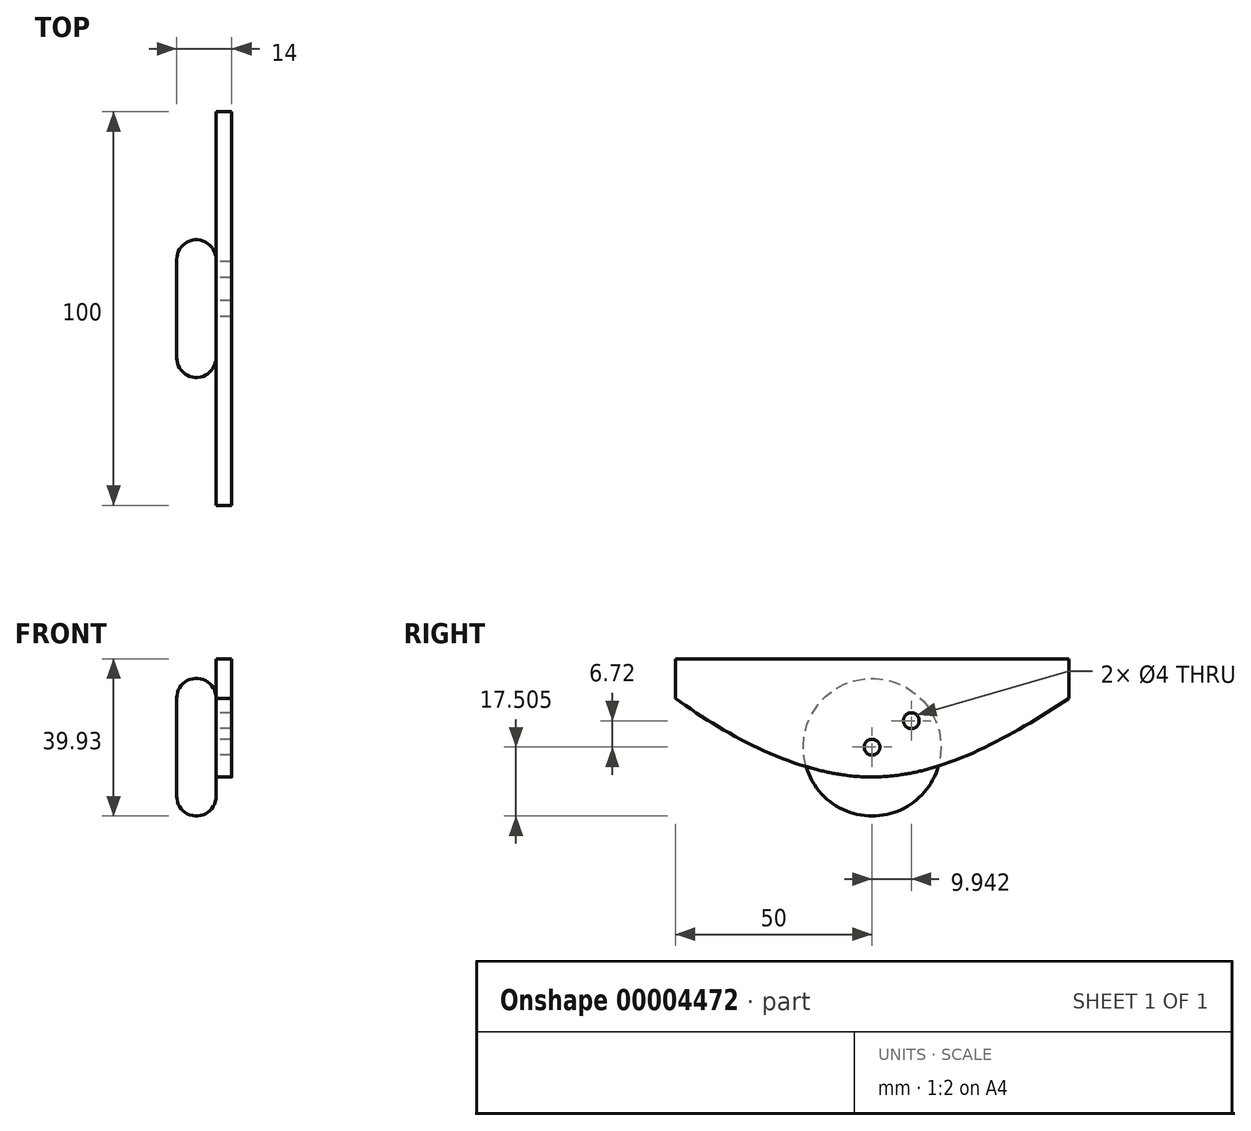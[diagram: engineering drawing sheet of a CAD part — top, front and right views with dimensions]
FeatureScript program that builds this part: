
annotation { "Feature Type Name" : "Feature", "Feature Type Description" : "" }
export const myFeature = defineFeature(function(context is Context, id is Id, definition is map)
    precondition{}
    {
        {
            var Q0;
            Q0=qCreatedBy(makeId("Right.planeOp"),FACE);
            var sketch = newSketch(context, id + "F0", { "sketchPlane" : qUnion([Q0])});
            skFitSpline(sketch, "E0", {"points": [v(-50, 0) * mm, v(0, -20) * mm, v(50, 0) * mm], "startDerivative": vector(87.23, -63) * mm, "endDerivative": vector(94.66, 62.2) * mm});
            skLineSegment(sketch, "E1", {"start": v(-50, 0) * mm, "end": v(-50, 10) * mm});
            skLineSegment(sketch, "E2", {"start": v(-50, 10) * mm, "end": v(50, 10) * mm});
            skLineSegment(sketch, "E3", {"start": v(50, 10) * mm, "end": v(50, 0) * mm});
            skCircle(sketch, "E4", {"center": v(0, -12.43) * mm, "radius": 17.5 * mm});
            skCircle(sketch, "E5", {"center": v(0, -12.43) * mm, "radius": 2 * mm});
            skCircle(sketch, "E6", {"center": v(0, -12.43) * mm, "radius": 10 * mm});
            skCircle(sketch, "E7", {"center": v(9.94, -5.7) * mm, "radius": 2 * mm});
            skCircle(sketch, "E8", {"center": v(9.94, -5.7) * mm, "radius": 1.25 * mm});
            skPoint(sketch, "E9", {"position": v(0, 10) * mm});
            skSolve(sketch);
        }
        {
            var Q0;
            {var subQ4=sQuery(id+"F0.wireOp",EDGE,"E1");Q0=makeQuery(id+"F0.imprint","IMPRINT",FACE,{"disambiguationData":[TD([[makeQuery(id+"F0.imprint","IMPRINT",EDGE,{"derivedFrom":subQ4}),-1.0]])]});}
            var Q1;
            {var subQ0=sQuery(id+"F0.wireOp",EDGE,"E7");Q1=makeQuery(id+"F0.imprint","IMPRINT",FACE,{"disambiguationData":[TD([[makeQuery(id+"F0.imprint","IMPRINT",EDGE,{"derivedFrom":subQ0}),-1.0]])]});}
            var Q2;
            Q2=makeQuery(id+"F0.imprint","IMPRINT",FACE,{"disambiguationData":[TD([[makeQuery(id+"F0.imprint","IMPRINT",EDGE,{"derivedFrom":sQuery(id+"F0.wireOp",EDGE,"E5")}),-1.0]])]});
            extrude(context, id + "F1", {"entities" : qUnion([Q0, Q1, Q2]), "depth" : 4 * mm});
        }
        {
            var Q0;
            Q0=makeQuery(id+"F0.imprint","IMPRINT",FACE,{"disambiguationData":[TD([[makeQuery(id+"F0.imprint","IMPRINT",EDGE,{"derivedFrom":sQuery(id+"F0.wireOp",EDGE,"E5")}),1.0]])]});
            var Q1;
            {var subQ0=sQuery(id+"F0.wireOp",EDGE,"E6");var subQ1=sQuery(id+"F0.wireOp",EDGE,"E0");var subQ3=makeQuery(id+"F0.imprint","INTERSECT",VERTEX,{"disambiguationData":[OD(0.0)],"derivedFrom":[subQ1,subQ0]});Q1=makeQuery(id+"F0.imprint","IMPRINT",FACE,{"disambiguationData":[TD([[makeQuery(id+"F0.imprint","IMPRINT",EDGE,{"disambiguationData":[TD([[subQ3,-1.0]])],"derivedFrom":subQ1}),-1.0]])]});}
            var Q2;
            {var subQ0=sQuery(id+"F0.wireOp",EDGE,"E7");Q2=makeQuery(id+"F0.imprint","IMPRINT",FACE,{"disambiguationData":[TD([[makeQuery(id+"F0.imprint","IMPRINT",EDGE,{"derivedFrom":subQ0}),-1.0]])]});}
            var Q3;
            {var subQ0=sQuery(id+"F0.wireOp",EDGE,"E4");var subQ1=sQuery(id+"F0.wireOp",EDGE,"E0");var subQ3=makeQuery(id+"F0.imprint","INTERSECT",VERTEX,{"disambiguationData":[OD(0.0)],"derivedFrom":[subQ1,subQ0]});Q3=makeQuery(id+"F0.imprint","IMPRINT",FACE,{"disambiguationData":[TD([[makeQuery(id+"F0.imprint","IMPRINT",EDGE,{"disambiguationData":[TD([[subQ3,-1.0]])],"derivedFrom":subQ1}),-1.0]])]});}
            var Q4;
            Q4=makeQuery(id+"F0.imprint","IMPRINT",FACE,{"disambiguationData":[TD([[makeQuery(id+"F0.imprint","IMPRINT",EDGE,{"derivedFrom":sQuery(id+"F0.wireOp",EDGE,"E5")}),-1.0]])]});
            var Q5;
            Q5=makeQuery(id+"F0.imprint","IMPRINT",FACE,{"disambiguationData":[TD([[makeQuery(id+"F0.imprint","IMPRINT",EDGE,{"derivedFrom":sQuery(id+"F0.wireOp",EDGE,"E8")}),1.0]])]});
            var Q6;
            Q6=makeQuery(id+"F0.imprint","IMPRINT",FACE,{"disambiguationData":[TD([[makeQuery(id+"F0.imprint","IMPRINT",EDGE,{"derivedFrom":sQuery(id+"F0.wireOp",EDGE,"E7")}),1.0]])]});
            var Q7;
            Q7=sQuery(id+"F0.wireOp",EDGE,"E4");
            extrude(context, id + "F2", {"entities" : qUnion([Q0, Q1, Q2, Q3, Q4, Q5, Q6]), "surfaceEntities" : qUnion([Q7]), "oppositeDirection" : true, "depth" : 10 * mm});
        }
        {
            var Q0;
            Q0=makeQuery(id+"F2.opExtrude","CAP_FACE",FACE,{"disambiguationData":[OSD([sQuery(id+"F0.wireOp",EDGE,"E4")])],"isStart":false});
            fillet(context, id + "F3", {"entities" : qUnion([Q0]), "radius" : 5 * mm, "tangentPropagation" : true, "allowEdgeOverflow" : false});
        }
        {
            var Q0;
            Q0=makeQuery(id+"F2.opExtrude","SWEPT_FACE",FACE,{"disambiguationData":[OSD([sQuery(id+"F0.wireOp",EDGE,"E4")])]});
            fillet(context, id + "F4", {"entities" : qUnion([Q0]), "radius" : 5 * mm, "tangentPropagation" : true, "allowEdgeOverflow" : false});
        }
    });
